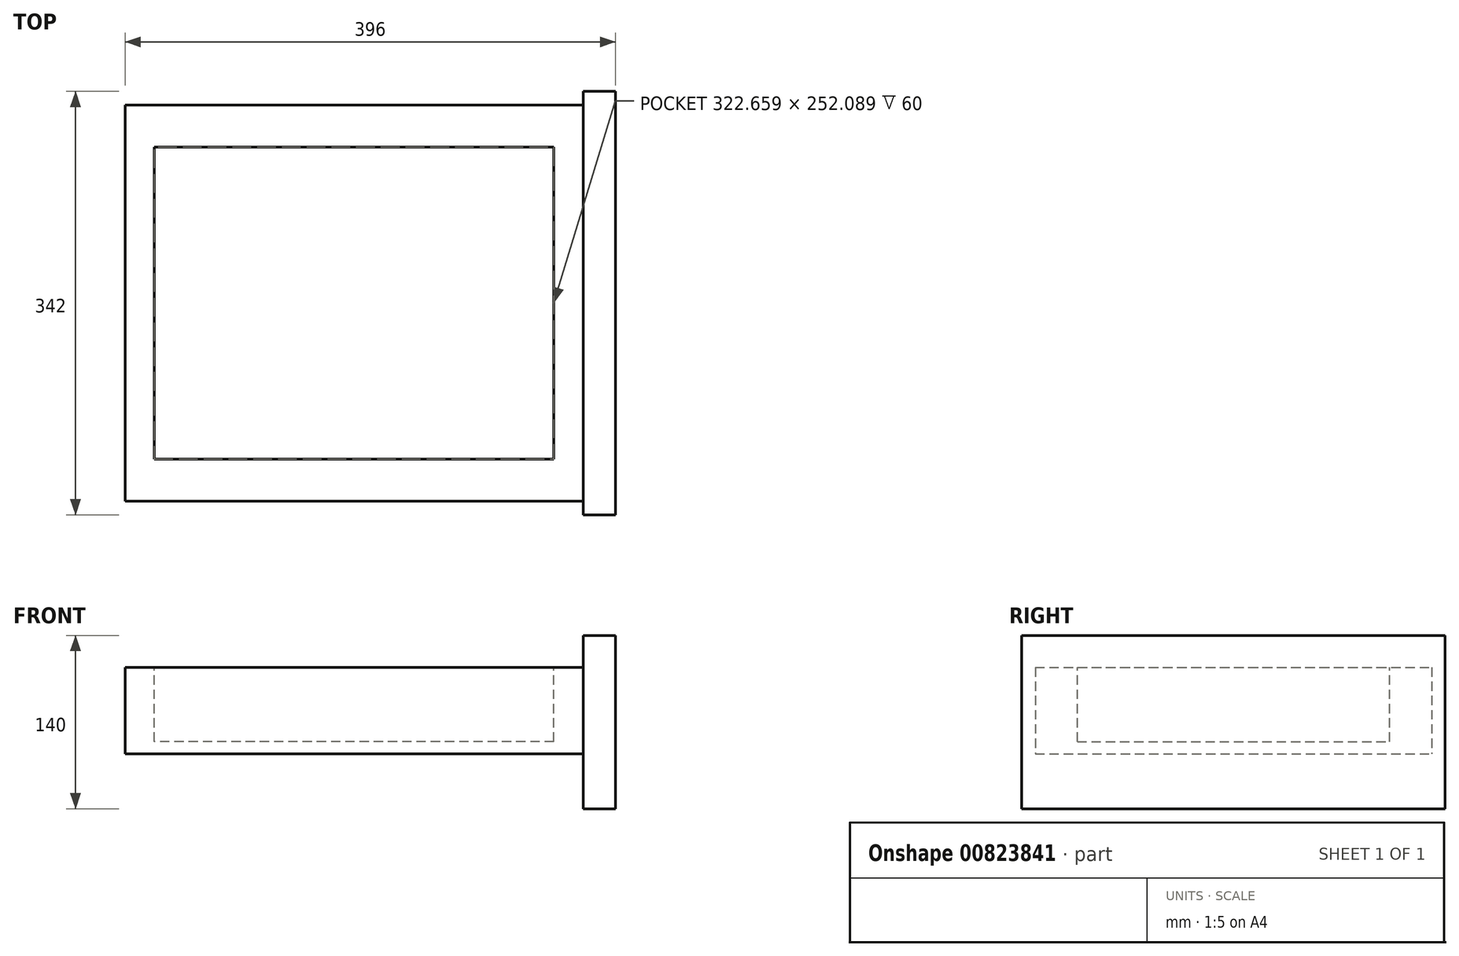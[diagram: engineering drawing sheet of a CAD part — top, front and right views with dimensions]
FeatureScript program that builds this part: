
annotation { "Feature Type Name" : "Feature", "Feature Type Description" : "" }
export const myFeature = defineFeature(function(context is Context, id is Id, definition is map)
    precondition{}
    {
        {
            var Q0;
            Q0=qCreatedBy(makeId("Top.planeOp"),FACE);
            var sketch = newSketch(context, id + "F0", { "sketchPlane" : qUnion([Q0])});
            skLineSegment(sketch, "E0.bottom", {"start": v(185, -160) * mm, "end": v(-185, -160) * mm});
            skLineSegment(sketch, "E0.top", {"start": v(185, 160) * mm, "end": v(-185, 160) * mm});
            skLineSegment(sketch, "E0.left", {"start": v(185, -160) * mm, "end": v(185, 160) * mm});
            skLineSegment(sketch, "E0.right", {"start": v(-185, -160) * mm, "end": v(-185, 160) * mm});
            skPoint(sketch, "E0.middle", {"position": v(0, 0) * mm});
            skSolve(sketch);
        }
        {
            var Q0;
            Q0=makeQuery(id+"F0.imprint","IMPRINT",FACE,{"disambiguationData":[TD([[makeQuery(id+"F0.imprint","IMPRINT",EDGE,{"derivedFrom":sQuery(id+"F0.wireOp",EDGE,"E0.bottom")}),-1.0]])]});
            extrude(context, id + "F1", {"entities" : qUnion([Q0]), "depth" : 70 * mm, "offsetDistance" : 25 * mm});
        }
        {
            var Q0;
            Q0=makeQuery(id+"F1.opExtrude","CAP_FACE",FACE,{"disambiguationData":[OSD([sQuery(id+"F0.wireOp",EDGE,"E0.bottom"),sQuery(id+"F0.wireOp",EDGE,"E0.top"),sQuery(id+"F0.wireOp",EDGE,"E0.left"),sQuery(id+"F0.wireOp",EDGE,"E0.right")])],"isStart":false});
            var sketch = newSketch(context, id + "F2", { "sketchPlane" : qUnion([Q0])});
            skLineSegment(sketch, "E1.bottom", {"start": v(161.33, -126.04) * mm, "end": v(-161.33, -126.04) * mm});
            skLineSegment(sketch, "E1.top", {"start": v(161.33, 126.04) * mm, "end": v(-161.33, 126.04) * mm});
            skLineSegment(sketch, "E1.left", {"start": v(161.33, -126.04) * mm, "end": v(161.33, 126.04) * mm});
            skLineSegment(sketch, "E1.right", {"start": v(-161.33, -126.04) * mm, "end": v(-161.33, 126.04) * mm});
            skPoint(sketch, "E1.middle", {"position": v(0, 0) * mm});
            skSolve(sketch);
        }
        {
            var Q0;
            Q0=makeQuery(id+"F2.imprint","IMPRINT",FACE,{"disambiguationData":[TD([[makeQuery(id+"F2.imprint","IMPRINT",EDGE,{"derivedFrom":sQuery(id+"F2.wireOp",EDGE,"E1.bottom")}),-1.0]])]});
            extrude(context, id + "F3", {"entities" : qUnion([Q0]), "operationType" : NewBodyOperationType.REMOVE, "oppositeDirection" : true, "depth" : 60 * mm, "offsetDistance" : 25 * mm});
        }
        {
            var Q0;
            Q0=makeQuery(id+"F1.opExtrude","SWEPT_FACE",FACE,{"disambiguationData":[OSD([sQuery(id+"F0.wireOp",EDGE,"E0.left")])]});
            var sketch = newSketch(context, id + "F4", { "sketchPlane" : qUnion([Q0])});
            skLineSegment(sketch, "E2.bottom", {"start": v(171, -44.18) * mm, "end": v(-171, -44.18) * mm});
            skLineSegment(sketch, "E2.top", {"start": v(171, 95.82) * mm, "end": v(-171, 95.82) * mm});
            skLineSegment(sketch, "E2.left", {"start": v(171, -44.18) * mm, "end": v(171, 95.82) * mm});
            skLineSegment(sketch, "E2.right", {"start": v(-171, -44.18) * mm, "end": v(-171, 95.82) * mm});
            skPoint(sketch, "E2.middle", {"position": v(0, 25.82) * mm});
            skSolve(sketch);
        }
        {
            var Q0;
            Q0 = qSketchRegion(id + "F4", true);
            extrude(context, id + "F5", {"entities" : qUnion([Q0]), "operationType" : NewBodyOperationType.ADD, "depth" : 26 * mm, "offsetDistance" : 25 * mm});
        }
    });
